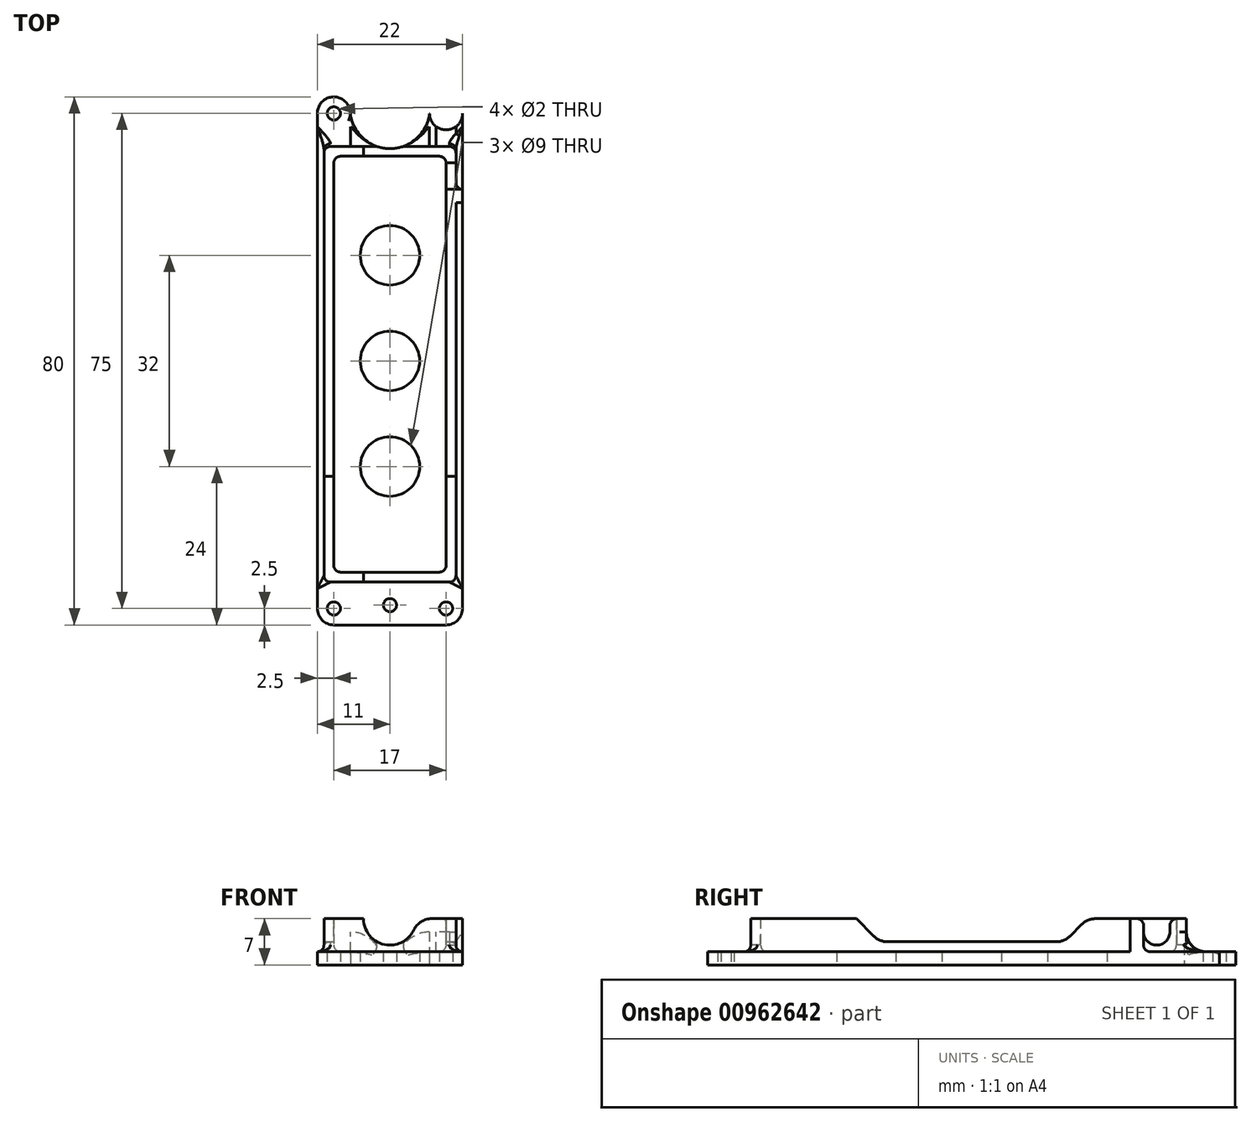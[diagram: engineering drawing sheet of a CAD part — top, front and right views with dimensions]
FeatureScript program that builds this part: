
annotation { "Feature Type Name" : "Feature", "Feature Type Description" : "" }
export const myFeature = defineFeature(function(context is Context, id is Id, definition is map)
    precondition{}
    {
        {
            var Q0;
            Q0=qCreatedBy(makeId("Top.planeOp"),FACE);
            var sketch = newSketch(context, id + "F0", { "sketchPlane" : qUnion([Q0])});
            skPoint(sketch, "E0.middle", {"position": v(0, 0) * mm});
            skPoint(sketch, "E1", {"position": v(-8, 8) * mm});
            skPoint(sketch, "E2", {"position": v(8, 8) * mm});
            skPoint(sketch, "E3", {"position": v(8, -8) * mm});
            skPoint(sketch, "E4", {"position": v(-8, -8) * mm});
            skLineSegment(sketch, "E5", {"start": v(0, -40) * mm, "end": v(8.5, -40) * mm});
            skLineSegment(sketch, "E6", {"start": v(11, -37.5) * mm, "end": v(11, -25.31) * mm});
            skLineSegment(sketch, "E7", {"start": v(-11, 37.5) * mm, "end": v(-11, 25.31) * mm});
            skLineSegment(sketch, "E8", {"start": v(-8.5, -40) * mm, "end": v(0, -40) * mm});
            skLineSegment(sketch, "E9.trimOffspring", {"start": v(11, 25.31) * mm, "end": v(11, 37.5) * mm});
            skLineSegment(sketch, "E10.trimOffspring", {"start": v(-11, -25.31) * mm, "end": v(-11, -37.5) * mm});
            skArc(sketch, "E11.filletArc", {"start": v(-8.5, 40) * mm, "mid": v(-10.27, 39.27) * mm, "end": v(-11, 37.5) * mm});
            skPoint(sketch, "E12.visualSharp", {"position": v(11, 40) * mm});
            skArc(sketch, "E12.filletArc", {"start": v(11, 37.5) * mm, "mid": v(10.27, 39.27) * mm, "end": v(8.5, 40) * mm});
            skArc(sketch, "E13.filletArc", {"start": v(-11, -37.5) * mm, "mid": v(-10.27, -39.27) * mm, "end": v(-8.5, -40) * mm});
            skPoint(sketch, "E14.visualSharp", {"position": v(11, -40) * mm});
            skArc(sketch, "E14.filletArc", {"start": v(8.5, -40) * mm, "mid": v(10.27, -39.27) * mm, "end": v(11, -37.5) * mm});
            skCircle(sketch, "E15", {"center": v(-8.5, 37.5) * mm, "radius": 2.5 * mm});
            skCircle(sketch, "E16", {"center": v(8.5, 37.5) * mm, "radius": 2.5 * mm});
            skCircle(sketch, "E17", {"center": v(-8.5, -37.5) * mm, "radius": 2.5 * mm});
            skCircle(sketch, "E18", {"center": v(8.5, -37.5) * mm, "radius": 2.5 * mm});
            skPoint(sketch, "E19", {"position": v(0, 16) * mm});
            skPoint(sketch, "E20.MirrorP", {"position": v(0, -16) * mm});
            skLineSegment(sketch, "E21", {"start": v(-11, 25.31) * mm, "end": v(-11, -25.31) * mm});
            skLineSegment(sketch, "E22", {"start": v(11, 25.31) * mm, "end": v(11, -25.31) * mm});
            skArc(sketch, "E23", {"start": v(-6, 37.43) * mm, "mid": v(0, 32.15) * mm, "end": v(6, 37.43) * mm});
            skPoint(sketch, "E23.centerSnap0", {"position": v(0, 40) * mm});
            skPoint(sketch, "E24", {"position": v(0, -37) * mm});
            skPoint(sketch, "E25", {"position": v(0, -32) * mm});
            skPoint(sketch, "E26", {"position": v(0, 31) * mm});
            skLineSegment(sketch, "E27", {"start": v(8.5, -32) * mm, "end": v(8.5, 31) * mm});
            skLineSegment(sketch, "E28", {"start": v(0, -32) * mm, "end": v(-8.5, -32) * mm});
            skLineSegment(sketch, "E29", {"start": v(-8.5, -32) * mm, "end": v(-8.5, 31) * mm});
            skLineSegment(sketch, "E30", {"start": v(-8.5, 31) * mm, "end": v(8.5, 31) * mm});
            skLineSegment(sketch, "E31", {"start": v(0, -32) * mm, "end": v(8.5, -32) * mm});
            skLineSegment(sketch, "E32", {"start": v(0, -33.5) * mm, "end": v(10, -33.5) * mm});
            skLineSegment(sketch, "E33", {"start": v(10, -33.5) * mm, "end": v(10, 32.5) * mm});
            skLineSegment(sketch, "E34", {"start": v(10, 32.5) * mm, "end": v(2.03, 32.5) * mm});
            skLineSegment(sketch, "E35.MirrorCS", {"start": v(-10, 32.5) * mm, "end": v(-2.03, 32.5) * mm});
            skLineSegment(sketch, "E36.MirrorCS", {"start": v(-10, -33.5) * mm, "end": v(-10, 32.5) * mm});
            skLineSegment(sketch, "E37.MirrorCS", {"start": v(0, -33.5) * mm, "end": v(-10, -33.5) * mm});
            skPoint(sketch, "E38.orphan", {"position": v(0, 32.5) * mm});
            skSolve(sketch);
        }
        {
            var Q0;
            {var subQ0=sQuery(id+"F0.wireOp",EDGE,"E15");var subQ1=makeQuery(id+"F0.imprint","INTERSECT",VERTEX,{"derivedFrom":[sQuery(id+"F0.wireOp",EDGE,"E7"),subQ0]});Q0=makeQuery(id+"F0.imprint","IMPRINT",FACE,{"disambiguationData":[TD([[makeQuery(id+"F0.imprint","IMPRINT",EDGE,{"disambiguationData":[TD([[subQ1,-1.0]])],"derivedFrom":subQ0}),1.0]])]});}
            var Q1;
            {var subQ3=sQuery(id+"F0.wireOp",EDGE,"E23");Q1=makeQuery(id+"F0.imprint","IMPRINT",FACE,{"disambiguationData":[TD([[makeQuery(id+"F0.imprint","IMPRINT",EDGE,{"derivedFrom":subQ3}),-1.0]])]});}
            var Q2;
            {var subQ0=sQuery(id+"F0.wireOp",EDGE,"E16");var subQ1=makeQuery(id+"F0.imprint","INTERSECT",VERTEX,{"derivedFrom":[sQuery(id+"F0.wireOp",EDGE,"E9.trimOffspring"),subQ0]});Q2=makeQuery(id+"F0.imprint","IMPRINT",FACE,{"disambiguationData":[TD([[makeQuery(id+"F0.imprint","IMPRINT",EDGE,{"disambiguationData":[TD([[subQ1,-1.0]])],"derivedFrom":subQ0}),1.0]])]});}
            var Q3;
            {var subQ3=sQuery(id+"F0.wireOp",EDGE,"E21");Q3=makeQuery(id+"F0.imprint","IMPRINT",FACE,{"disambiguationData":[TD([[makeQuery(id+"F0.imprint","IMPRINT",EDGE,{"derivedFrom":subQ3}),1.0]])]});}
            var Q4;
            Q4=makeQuery(id+"F0.imprint","IMPRINT",FACE,{"disambiguationData":[TD([[makeQuery(id+"F0.imprint","IMPRINT",EDGE,{"derivedFrom":sQuery(id+"F0.wireOp",EDGE,"bMtfzaGi-QSrd-IoLL-XQbp-31UsCRVkDCwl")}),1.0]])]});
            var Q5;
            {var subQ9=sQuery(id+"F0.wireOp",EDGE,"E5");Q5=makeQuery(id+"F0.imprint","IMPRINT",FACE,{"disambiguationData":[TD([[makeQuery(id+"F0.imprint","IMPRINT",EDGE,{"derivedFrom":subQ9}),1.0]])]});}
            var Q6;
            {var subQ0=sQuery(id+"F0.wireOp",EDGE,"E17");var subQ1=makeQuery(id+"F0.imprint","INTERSECT",VERTEX,{"derivedFrom":[sQuery(id+"F0.wireOp",EDGE,"E8"),subQ0]});Q6=makeQuery(id+"F0.imprint","IMPRINT",FACE,{"disambiguationData":[TD([[makeQuery(id+"F0.imprint","IMPRINT",EDGE,{"disambiguationData":[TD([[subQ1,1.0]])],"derivedFrom":subQ0}),1.0]])]});}
            var Q7;
            {var subQ0=sQuery(id+"F0.wireOp",EDGE,"E18");var subQ1=makeQuery(id+"F0.imprint","INTERSECT",VERTEX,{"derivedFrom":[sQuery(id+"F0.wireOp",EDGE,"E5"),subQ0]});Q7=makeQuery(id+"F0.imprint","IMPRINT",FACE,{"disambiguationData":[TD([[makeQuery(id+"F0.imprint","IMPRINT",EDGE,{"disambiguationData":[TD([[subQ1,1.0]])],"derivedFrom":subQ0}),1.0]])]});}
            var Q8;
            Q8=makeQuery(id+"F0.imprint","IMPRINT",FACE,{"disambiguationData":[TD([[makeQuery(id+"F0.imprint","IMPRINT",EDGE,{"derivedFrom":sQuery(id+"F0.wireOp",EDGE,"E27")}),-1.0]])]});
            var Q9;
            Q9=makeQuery(id+"F0.imprint","IMPRINT",FACE,{"disambiguationData":[TD([[makeQuery(id+"F0.imprint","IMPRINT",EDGE,{"derivedFrom":sQuery(id+"F0.wireOp",EDGE,"E27")}),1.0]])]});
            extrude(context, id + "F1", {"entities" : qUnion([Q0, Q1, Q2, Q3, Q4, Q5, Q6, Q7, Q8, Q9]), "depth" : 2 * mm, "offsetDistance" : 25 * mm});
        }
        {
            var Q0;
            Q0=makeQuery(id+"F0.imprint","IMPRINT",FACE,{"disambiguationData":[TD([[makeQuery(id+"F0.imprint","IMPRINT",EDGE,{"derivedFrom":sQuery(id+"F0.wireOp",EDGE,"E27")}),-1.0]])]});
            extrude(context, id + "F2", {"entities" : qUnion([Q0]), "operationType" : NewBodyOperationType.ADD, "depth" : 7 * mm, "offsetDistance" : 25 * mm});
        }
        {
            var Q0;
            Q0=makeQuery(id+"F1.opExtrude","CAP_EDGE",EDGE,{"disambiguationData":[OSD([sQuery(id+"F0.wireOp",EDGE,"E23")])],"isStart":false});
            fillet(context, id + "F3", {"entities" : qUnion([Q0]), "radius" : 0.5 * mm, "tangentPropagation" : true, "allowEdgeOverflow" : false});
        }
        {
            var Q0;
            Q0=makeQuery(id+"F2.opExtrude","SWEPT_EDGE",EDGE,{"disambiguationData":[OSD([sQuery(id+"F0.wireOp",EDGE,"tbeNza1r-utGL-zFzt-WYe0-U05ca4cfrUVO"),sQuery(id+"F0.wireOp",EDGE,"CjghIOQ9-IqcJ-TMon-Jhqv-waYeZpEdJ196")])]});
            var Q1;
            Q1=makeQuery(id+"F2.opExtrude","SWEPT_EDGE",EDGE,{"disambiguationData":[OSD([sQuery(id+"F0.wireOp",EDGE,"bMtfzaGi-QSrd-IoLL-XQbp-31UsCRVkDCwl"),sQuery(id+"F0.wireOp",EDGE,"sX6MG20U-e8zL-cwBF-vJcw-WzJNnX85c195")])]});
            var Q2;
            Q2=makeQuery(id+"F2.opExtrude","SWEPT_EDGE",EDGE,{"disambiguationData":[OSD([sQuery(id+"F0.wireOp",EDGE,"sX6MG20U-e8zL-cwBF-vJcw-WzJNnX85c195"),sQuery(id+"F0.wireOp",EDGE,"Iet94KMb-kpEY-E7AR-qc5a-OqAxkwTAn5af")])]});
            var Q3;
            Q3=makeQuery(id+"F2.opExtrude","SWEPT_EDGE",EDGE,{"disambiguationData":[OSD([sQuery(id+"F0.wireOp",EDGE,"Iet94KMb-kpEY-E7AR-qc5a-OqAxkwTAn5af"),sQuery(id+"F0.wireOp",EDGE,"tbeNza1r-utGL-zFzt-WYe0-U05ca4cfrUVO")])]});
            var Q4;
            Q4=makeQuery(id+"F2.boolean.opBoolean","INTERSECT",EDGE,{"derivedFrom":[makeQuery(id+"F1.opExtrude","CAP_FACE",FACE,{"disambiguationData":[OSD([sQuery(id+"F0.wireOp",EDGE,"E5"),sQuery(id+"F0.wireOp",EDGE,"E6"),sQuery(id+"F0.wireOp",EDGE,"E7"),sQuery(id+"F0.wireOp",EDGE,"E8"),sQuery(id+"F0.wireOp",EDGE,"E9.trimOffspring"),sQuery(id+"F0.wireOp",EDGE,"E10.trimOffspring"),sQuery(id+"F0.wireOp",EDGE,"E15"),sQuery(id+"F0.wireOp",EDGE,"E16"),sQuery(id+"F0.wireOp",EDGE,"E17"),sQuery(id+"F0.wireOp",EDGE,"E18"),sQuery(id+"F0.wireOp",EDGE,"E21"),sQuery(id+"F0.wireOp",EDGE,"E22"),sQuery(id+"F0.wireOp",EDGE,"E23")])],"isStart":false}),makeQuery(id+"F2.opExtrude","SWEPT_FACE",FACE,{"disambiguationData":[OSD([sQuery(id+"F0.wireOp",EDGE,"E27")])]})]});
            var Q5;
            Q5=makeQuery(id+"F2.boolean.opBoolean","INTERSECT",EDGE,{"derivedFrom":[makeQuery(id+"F1.opExtrude","CAP_FACE",FACE,{"disambiguationData":[OSD([sQuery(id+"F0.wireOp",EDGE,"E5"),sQuery(id+"F0.wireOp",EDGE,"E6"),sQuery(id+"F0.wireOp",EDGE,"E7"),sQuery(id+"F0.wireOp",EDGE,"E8"),sQuery(id+"F0.wireOp",EDGE,"E9.trimOffspring"),sQuery(id+"F0.wireOp",EDGE,"E10.trimOffspring"),sQuery(id+"F0.wireOp",EDGE,"E15"),sQuery(id+"F0.wireOp",EDGE,"E16"),sQuery(id+"F0.wireOp",EDGE,"E17"),sQuery(id+"F0.wireOp",EDGE,"E18"),sQuery(id+"F0.wireOp",EDGE,"E21"),sQuery(id+"F0.wireOp",EDGE,"E22"),sQuery(id+"F0.wireOp",EDGE,"E23")])],"isStart":false}),makeQuery(id+"F2.opExtrude","SWEPT_FACE",FACE,{"disambiguationData":[OSD([sQuery(id+"F0.wireOp",EDGE,"E28"),sQuery(id+"F0.wireOp",EDGE,"E31")])]})]});
            var Q6;
            Q6=makeQuery(id+"F2.boolean.opBoolean","INTERSECT",EDGE,{"derivedFrom":[makeQuery(id+"F1.opExtrude","CAP_FACE",FACE,{"disambiguationData":[OSD([sQuery(id+"F0.wireOp",EDGE,"E5"),sQuery(id+"F0.wireOp",EDGE,"E6"),sQuery(id+"F0.wireOp",EDGE,"E7"),sQuery(id+"F0.wireOp",EDGE,"E8"),sQuery(id+"F0.wireOp",EDGE,"E9.trimOffspring"),sQuery(id+"F0.wireOp",EDGE,"E10.trimOffspring"),sQuery(id+"F0.wireOp",EDGE,"E15"),sQuery(id+"F0.wireOp",EDGE,"E16"),sQuery(id+"F0.wireOp",EDGE,"E17"),sQuery(id+"F0.wireOp",EDGE,"E18"),sQuery(id+"F0.wireOp",EDGE,"E21"),sQuery(id+"F0.wireOp",EDGE,"E22"),sQuery(id+"F0.wireOp",EDGE,"E23")])],"isStart":false}),makeQuery(id+"F2.opExtrude","SWEPT_FACE",FACE,{"disambiguationData":[OSD([sQuery(id+"F0.wireOp",EDGE,"E29")])]})]});
            var Q7;
            Q7=makeQuery(id+"F2.boolean.opBoolean","INTERSECT",EDGE,{"derivedFrom":[makeQuery(id+"F1.opExtrude","CAP_FACE",FACE,{"disambiguationData":[OSD([sQuery(id+"F0.wireOp",EDGE,"E5"),sQuery(id+"F0.wireOp",EDGE,"E6"),sQuery(id+"F0.wireOp",EDGE,"E7"),sQuery(id+"F0.wireOp",EDGE,"E8"),sQuery(id+"F0.wireOp",EDGE,"E9.trimOffspring"),sQuery(id+"F0.wireOp",EDGE,"E10.trimOffspring"),sQuery(id+"F0.wireOp",EDGE,"E15"),sQuery(id+"F0.wireOp",EDGE,"E16"),sQuery(id+"F0.wireOp",EDGE,"E17"),sQuery(id+"F0.wireOp",EDGE,"E18"),sQuery(id+"F0.wireOp",EDGE,"E21"),sQuery(id+"F0.wireOp",EDGE,"E22"),sQuery(id+"F0.wireOp",EDGE,"E23")])],"isStart":false}),makeQuery(id+"F2.opExtrude","SWEPT_FACE",FACE,{"disambiguationData":[OSD([sQuery(id+"F0.wireOp",EDGE,"E30")])]})]});
            var Q8;
            Q8=makeQuery(id+"F2.boolean.opBoolean","INTERSECT",EDGE,{"derivedFrom":[makeQuery(id+"F1.opExtrude","CAP_FACE",FACE,{"disambiguationData":[OSD([sQuery(id+"F0.wireOp",EDGE,"E5"),sQuery(id+"F0.wireOp",EDGE,"E6"),sQuery(id+"F0.wireOp",EDGE,"E7"),sQuery(id+"F0.wireOp",EDGE,"E8"),sQuery(id+"F0.wireOp",EDGE,"E9.trimOffspring"),sQuery(id+"F0.wireOp",EDGE,"E10.trimOffspring"),sQuery(id+"F0.wireOp",EDGE,"E15"),sQuery(id+"F0.wireOp",EDGE,"E16"),sQuery(id+"F0.wireOp",EDGE,"E17"),sQuery(id+"F0.wireOp",EDGE,"E18"),sQuery(id+"F0.wireOp",EDGE,"E21"),sQuery(id+"F0.wireOp",EDGE,"E22"),sQuery(id+"F0.wireOp",EDGE,"E23")])],"isStart":false}),makeQuery(id+"F2.opExtrude","SWEPT_FACE",FACE,{"disambiguationData":[OSD([sQuery(id+"F0.wireOp",EDGE,"E32"),sQuery(id+"F0.wireOp",EDGE,"E37.MirrorCS")])]})]});
            var Q9;
            Q9=makeQuery(id+"F2.boolean.opBoolean","INTERSECT",EDGE,{"derivedFrom":[makeQuery(id+"F1.opExtrude","CAP_FACE",FACE,{"disambiguationData":[OSD([sQuery(id+"F0.wireOp",EDGE,"E5"),sQuery(id+"F0.wireOp",EDGE,"E6"),sQuery(id+"F0.wireOp",EDGE,"E7"),sQuery(id+"F0.wireOp",EDGE,"E8"),sQuery(id+"F0.wireOp",EDGE,"E9.trimOffspring"),sQuery(id+"F0.wireOp",EDGE,"E10.trimOffspring"),sQuery(id+"F0.wireOp",EDGE,"E15"),sQuery(id+"F0.wireOp",EDGE,"E16"),sQuery(id+"F0.wireOp",EDGE,"E17"),sQuery(id+"F0.wireOp",EDGE,"E18"),sQuery(id+"F0.wireOp",EDGE,"E21"),sQuery(id+"F0.wireOp",EDGE,"E22"),sQuery(id+"F0.wireOp",EDGE,"E23")])],"isStart":false}),makeQuery(id+"F2.opExtrude","SWEPT_FACE",FACE,{"disambiguationData":[OSD([sQuery(id+"F0.wireOp",EDGE,"E33")])]})]});
            var Q10;
            Q10=makeQuery(id+"F2.boolean.opBoolean","INTERSECT",EDGE,{"derivedFrom":[makeQuery(id+"F1.opExtrude","CAP_FACE",FACE,{"disambiguationData":[OSD([sQuery(id+"F0.wireOp",EDGE,"E5"),sQuery(id+"F0.wireOp",EDGE,"E6"),sQuery(id+"F0.wireOp",EDGE,"E7"),sQuery(id+"F0.wireOp",EDGE,"E8"),sQuery(id+"F0.wireOp",EDGE,"E9.trimOffspring"),sQuery(id+"F0.wireOp",EDGE,"E10.trimOffspring"),sQuery(id+"F0.wireOp",EDGE,"E15"),sQuery(id+"F0.wireOp",EDGE,"E16"),sQuery(id+"F0.wireOp",EDGE,"E17"),sQuery(id+"F0.wireOp",EDGE,"E18"),sQuery(id+"F0.wireOp",EDGE,"E21"),sQuery(id+"F0.wireOp",EDGE,"E22"),sQuery(id+"F0.wireOp",EDGE,"E23")])],"isStart":false}),makeQuery(id+"F2.opExtrude","SWEPT_FACE",FACE,{"disambiguationData":[OSD([sQuery(id+"F0.wireOp",EDGE,"E36.MirrorCS")])]})]});
            fillet(context, id + "F4", {"entities" : qUnion([Q0, Q1, Q2, Q3, Q4, Q5, Q6, Q7, Q8, Q9, Q10]), "radius" : 1 * mm, "tangentPropagation" : true, "allowEdgeOverflow" : false});
        }
        {
            var Q0;
            Q0=makeQuery(id+"F2.opExtrude","SWEPT_FACE",FACE,{"disambiguationData":[OSD([sQuery(id+"F0.wireOp",EDGE,"E36.MirrorCS")])]});
            var sketch = newSketch(context, id + "F5", { "sketchPlane" : qUnion([Q0])});
            skLineSegment(sketch, "E39", {"start": v(0, 0) * mm, "end": v(0, 3.5) * mm});
            skLineSegment(sketch, "E40", {"start": v(0, 3.5) * mm, "end": v(14, 3.5) * mm});
            skLineSegment(sketch, "E41", {"start": v(17.5, 7) * mm, "end": v(14, 3.5) * mm});
            skLineSegment(sketch, "E42.MirrorCS", {"start": v(0, 3.5) * mm, "end": v(-14, 3.5) * mm});
            skLineSegment(sketch, "E43.MirrorCS", {"start": v(-17.5, 7) * mm, "end": v(-14, 3.5) * mm});
            skSolve(sketch);
        }
        {
            var Q0;
            Q0=makeQuery(id+"F5.imprint","IMPRINT",FACE,{"disambiguationData":[TD([[makeQuery(id+"F5.imprint","IMPRINT",EDGE,{"derivedFrom":sQuery(id+"F5.wireOp",EDGE,"E40")}),1.0]])]});
            extrude(context, id + "F6", {"entities" : qUnion([Q0]), "operationType" : NewBodyOperationType.REMOVE, "depth" : 25 * mm, "offsetDistance" : 25 * mm, "hasSecondDirection" : true, "secondDirectionOppositeDirection" : true, "secondDirectionDepth" : 25 * mm});
        }
        {
            var Q0;
            Q0=sQuery(id+"F0.wireOp",VERTEX,"E12.filletArc.center");
            var Q1;
            Q1=sQuery(id+"F0.wireOp",VERTEX,"E11.filletArc.center");
            var Q2;
            Q2=sQuery(id+"F0.wireOp",VERTEX,"E14.filletArc.center");
            var Q3;
            Q3=sQuery(id+"F0.wireOp",VERTEX,"E13.filletArc.center");
            var Q4;
            Q4=sQuery(id+"F0.wireOp",VERTEX,"E24");
            var Q5;
            Q5=makeQuery(id+"F1.opExtrude","SWEPT_BODY",BODY,{"disambiguationData":[OSD([sQuery(id+"F0.wireOp",EDGE,"E5"),sQuery(id+"F0.wireOp",EDGE,"E6"),sQuery(id+"F0.wireOp",EDGE,"E7"),sQuery(id+"F0.wireOp",EDGE,"E8"),sQuery(id+"F0.wireOp",EDGE,"E9.trimOffspring"),sQuery(id+"F0.wireOp",EDGE,"E10.trimOffspring"),sQuery(id+"F0.wireOp",EDGE,"E15"),sQuery(id+"F0.wireOp",EDGE,"E16"),sQuery(id+"F0.wireOp",EDGE,"E17"),sQuery(id+"F0.wireOp",EDGE,"E18"),sQuery(id+"F0.wireOp",EDGE,"E21"),sQuery(id+"F0.wireOp",EDGE,"E22"),sQuery(id+"F0.wireOp",EDGE,"E23")])]});
            hole(context, id + "F7", {"style" : HoleStyle.SIMPLE, "endStyle" : HoleEndStyle.BLIND, "oppositeDirection" : true, "holeDiameter" : 2 * mm, "majorDiameter" : 5 * mm, "holeDepth" : 7 * mm, "isTappedThrough" : true, "tappedDepth" : 12 * mm, "tapClearance" : 3, "startFromSketch" : true, "locations" : qUnion([Q0, Q1, Q2, Q3, Q4]), "scope" : qUnion([Q5])});
        }
        {
            var Q0;
            Q0=sQuery(id+"F0.wireOp",VERTEX,"E19");
            var Q1;
            Q1=sQuery(id+"F0.wireOp",VERTEX,"E20.MirrorP");
            var Q2;
            Q2=sQuery(id+"F0.wireOp",VERTEX,"E0.middle");
            var Q3;
            Q3=makeQuery(id+"F1.opExtrude","SWEPT_BODY",BODY,{"disambiguationData":[OSD([sQuery(id+"F0.wireOp",EDGE,"E5"),sQuery(id+"F0.wireOp",EDGE,"E6"),sQuery(id+"F0.wireOp",EDGE,"E7"),sQuery(id+"F0.wireOp",EDGE,"E8"),sQuery(id+"F0.wireOp",EDGE,"E9.trimOffspring"),sQuery(id+"F0.wireOp",EDGE,"E10.trimOffspring"),sQuery(id+"F0.wireOp",EDGE,"E15"),sQuery(id+"F0.wireOp",EDGE,"E16"),sQuery(id+"F0.wireOp",EDGE,"E17"),sQuery(id+"F0.wireOp",EDGE,"E18"),sQuery(id+"F0.wireOp",EDGE,"E21"),sQuery(id+"F0.wireOp",EDGE,"E22"),sQuery(id+"F0.wireOp",EDGE,"E23")])]});
            hole(context, id + "F8", {"style" : HoleStyle.SIMPLE, "endStyle" : HoleEndStyle.BLIND, "oppositeDirection" : true, "holeDiameter" : 9 * mm, "majorDiameter" : 5 * mm, "holeDepth" : 7 * mm, "isTappedThrough" : true, "tappedDepth" : 12 * mm, "tapClearance" : 3, "startFromSketch" : true, "locations" : qUnion([Q0, Q1, Q2]), "scope" : qUnion([Q3])});
        }
        {
            var Q0;
            Q0=makeQuery(id+"F2.boolean.opBoolean","INTERSECT",EDGE,{"derivedFrom":[makeQuery(id+"F1.opExtrude","CAP_FACE",FACE,{"disambiguationData":[OSD([sQuery(id+"F0.wireOp",EDGE,"E5"),sQuery(id+"F0.wireOp",EDGE,"E6"),sQuery(id+"F0.wireOp",EDGE,"E7"),sQuery(id+"F0.wireOp",EDGE,"E8"),sQuery(id+"F0.wireOp",EDGE,"E9.trimOffspring"),sQuery(id+"F0.wireOp",EDGE,"E10.trimOffspring"),sQuery(id+"F0.wireOp",EDGE,"E15"),sQuery(id+"F0.wireOp",EDGE,"E16"),sQuery(id+"F0.wireOp",EDGE,"E17"),sQuery(id+"F0.wireOp",EDGE,"E18"),sQuery(id+"F0.wireOp",EDGE,"E21"),sQuery(id+"F0.wireOp",EDGE,"E22"),sQuery(id+"F0.wireOp",EDGE,"E23")])],"isStart":false}),makeQuery(id+"F2.opExtrude","SWEPT_FACE",FACE,{"disambiguationData":[OSD([sQuery(id+"F0.wireOp",EDGE,"E35.MirrorCS")])]})]});
            var Q1;
            Q1=makeQuery(id+"F2.boolean.opBoolean","INTERSECT",EDGE,{"derivedFrom":[makeQuery(id+"F1.opExtrude","CAP_FACE",FACE,{"disambiguationData":[OSD([sQuery(id+"F0.wireOp",EDGE,"E5"),sQuery(id+"F0.wireOp",EDGE,"E6"),sQuery(id+"F0.wireOp",EDGE,"E7"),sQuery(id+"F0.wireOp",EDGE,"E8"),sQuery(id+"F0.wireOp",EDGE,"E9.trimOffspring"),sQuery(id+"F0.wireOp",EDGE,"E10.trimOffspring"),sQuery(id+"F0.wireOp",EDGE,"E15"),sQuery(id+"F0.wireOp",EDGE,"E16"),sQuery(id+"F0.wireOp",EDGE,"E17"),sQuery(id+"F0.wireOp",EDGE,"E18"),sQuery(id+"F0.wireOp",EDGE,"E21"),sQuery(id+"F0.wireOp",EDGE,"E22"),sQuery(id+"F0.wireOp",EDGE,"E23")])],"isStart":false}),makeQuery(id+"F2.opExtrude","SWEPT_FACE",FACE,{"disambiguationData":[OSD([sQuery(id+"F0.wireOp",EDGE,"E34")])]})]});
            fillet(context, id + "F9", {"entities" : qUnion([Q0, Q1]), "radius" : 3 * mm, "tangentPropagation" : true, "allowEdgeOverflow" : false});
        }
        {
            var Q0;
            Q0=makeQuery(id+"F2.opExtrude","SWEPT_FACE",FACE,{"disambiguationData":[OSD([sQuery(id+"F0.wireOp",EDGE,"E32"),sQuery(id+"F0.wireOp",EDGE,"E37.MirrorCS")])]});
            var sketch = newSketch(context, id + "F10", { "sketchPlane" : qUnion([Q0])});
            skLineSegment(sketch, "E44", {"start": v(0, 0) * mm, "end": v(0, 7) * mm});
            skCircle(sketch, "E45", {"center": v(0, 7) * mm, "radius": 4 * mm});
            skSolve(sketch);
        }
        {
            var Q0;
            {var subQ0=sQuery(id+"F10.wireOp",EDGE,"E44");var subQ1=sQuery(id+"F0.wireOp",EDGE,"E37.MirrorCS");var subQ2=sQuery(id+"F0.wireOp",EDGE,"E32");var subQ3=makeQuery(id+"F2.opExtrude","CAP_EDGE",EDGE,{"disambiguationData":[OSD([subQ2,subQ1])],"isStart":false});var subQ4=makeQuery(id+"F10.imprint","INTERSECT",VERTEX,{"derivedFrom":[subQ3,subQ0]});Q0=makeQuery(id+"F10.imprint","IMPRINT",FACE,{"disambiguationData":[TD([[makeQuery(id+"F10.imprint","IMPRINT",EDGE,{"disambiguationData":[TD([[subQ4,-1.0]])],"derivedFrom":subQ3}),1.0]])]});}
            var Q1;
            {var subQ0=sQuery(id+"F10.wireOp",EDGE,"E44");var subQ1=sQuery(id+"F0.wireOp",EDGE,"E37.MirrorCS");var subQ2=sQuery(id+"F0.wireOp",EDGE,"E32");var subQ3=makeQuery(id+"F2.opExtrude","CAP_EDGE",EDGE,{"disambiguationData":[OSD([subQ2,subQ1])],"isStart":false});var subQ4=makeQuery(id+"F10.imprint","INTERSECT",VERTEX,{"derivedFrom":[subQ3,subQ0]});Q1=makeQuery(id+"F10.imprint","IMPRINT",FACE,{"disambiguationData":[TD([[makeQuery(id+"F10.imprint","IMPRINT",EDGE,{"disambiguationData":[TD([[subQ4,1.0]])],"derivedFrom":subQ3}),1.0]])]});}
            extrude(context, id + "F11", {"entities" : qUnion([Q0, Q1]), "operationType" : NewBodyOperationType.REMOVE, "oppositeDirection" : true, "depth" : 80 * mm, "offsetDistance" : 25 * mm});
        }
        {
            var Q0;
            {var subQ0=sQuery(id+"F0.wireOp",EDGE,"E37.MirrorCS");var subQ1=sQuery(id+"F0.wireOp",EDGE,"E32");var subQ2=sQuery(id+"F0.wireOp",EDGE,"E31");var subQ3=sQuery(id+"F0.wireOp",EDGE,"E28");var subQ4=sQuery(id+"F10.wireOp",EDGE,"E45");Q0=makeQuery(id+"F11.boolean.opBoolean","COPY",EDGE,{"disambiguationData":[TD([makeQuery(id+"F2.opExtrude","SWEPT_FACE",FACE,{"disambiguationData":[OSD([subQ3,subQ2])]})])],"derivedFrom":makeQuery(id+"F11.opExtrude","SWEPT_EDGE",EDGE,{"disambiguationData":[OSD([subQ1,subQ0,subQ4]),TDD([makeQuery(id+"F10.imprint","INTERSECT",VERTEX,{"disambiguationData":[OD(1.0)],"derivedFrom":[makeQuery(id+"F2.opExtrude","CAP_EDGE",EDGE,{"disambiguationData":[OSD([subQ1,subQ0])],"isStart":false}),subQ4]})])]})});}
            var Q1;
            {var subQ0=sQuery(id+"F0.wireOp",EDGE,"E37.MirrorCS");var subQ1=sQuery(id+"F0.wireOp",EDGE,"E32");var subQ2=sQuery(id+"F0.wireOp",EDGE,"E31");var subQ3=sQuery(id+"F0.wireOp",EDGE,"E28");var subQ4=sQuery(id+"F10.wireOp",EDGE,"E45");Q1=makeQuery(id+"F11.boolean.opBoolean","COPY",EDGE,{"disambiguationData":[TD([makeQuery(id+"F2.opExtrude","SWEPT_FACE",FACE,{"disambiguationData":[OSD([subQ3,subQ2])]})])],"derivedFrom":makeQuery(id+"F11.opExtrude","SWEPT_EDGE",EDGE,{"disambiguationData":[OSD([subQ1,subQ0,subQ4]),TDD([makeQuery(id+"F10.imprint","INTERSECT",VERTEX,{"disambiguationData":[OD(0.0)],"derivedFrom":[makeQuery(id+"F2.opExtrude","CAP_EDGE",EDGE,{"disambiguationData":[OSD([subQ1,subQ0])],"isStart":false}),subQ4]})])]})});}
            var Q2;
            {var subQ0=sQuery(id+"F0.wireOp",EDGE,"E36.MirrorCS");var subQ2=sQuery(id+"F0.wireOp",EDGE,"E27");var subQ3=sQuery(id+"F5.wireOp",EDGE,"E41");Q2=makeQuery(id+"F6.boolean.opBoolean","COPY",EDGE,{"disambiguationData":[TD([makeQuery(id+"F2.opExtrude","SWEPT_FACE",FACE,{"disambiguationData":[OSD([subQ2])]})])],"derivedFrom":makeQuery(id+"F6.opExtrude","SWEPT_EDGE",EDGE,{"disambiguationData":[OSD([subQ0,subQ3])]})});}
            var Q3;
            {var subQ0=sQuery(id+"F5.wireOp",EDGE,"E40");var subQ1=sQuery(id+"F5.wireOp",EDGE,"E41");Q3=makeQuery(id+"F6.boolean.opBoolean","COPY",EDGE,{"disambiguationData":[TD([makeQuery(id+"F2.opExtrude","SWEPT_FACE",FACE,{"disambiguationData":[OSD([sQuery(id+"F0.wireOp",EDGE,"E27")])]})])],"derivedFrom":makeQuery(id+"F6.opExtrude","SWEPT_EDGE",EDGE,{"disambiguationData":[OSD([subQ0,subQ1])]})});}
            var Q4;
            {var subQ0=sQuery(id+"F5.wireOp",EDGE,"E42.MirrorCS");var subQ1=sQuery(id+"F5.wireOp",EDGE,"E43.MirrorCS");Q4=makeQuery(id+"F6.boolean.opBoolean","COPY",EDGE,{"disambiguationData":[TD([makeQuery(id+"F2.opExtrude","SWEPT_FACE",FACE,{"disambiguationData":[OSD([sQuery(id+"F0.wireOp",EDGE,"E27")])]})])],"derivedFrom":makeQuery(id+"F6.opExtrude","SWEPT_EDGE",EDGE,{"disambiguationData":[OSD([subQ0,subQ1])]})});}
            var Q5;
            {var subQ0=sQuery(id+"F0.wireOp",EDGE,"E36.MirrorCS");var subQ2=sQuery(id+"F0.wireOp",EDGE,"E27");var subQ3=sQuery(id+"F5.wireOp",EDGE,"E43.MirrorCS");Q5=makeQuery(id+"F6.boolean.opBoolean","COPY",EDGE,{"disambiguationData":[TD([makeQuery(id+"F2.opExtrude","SWEPT_FACE",FACE,{"disambiguationData":[OSD([subQ2])]})])],"derivedFrom":makeQuery(id+"F6.opExtrude","SWEPT_EDGE",EDGE,{"disambiguationData":[OSD([subQ0,subQ3])]})});}
            var Q6;
            {var subQ0=sQuery(id+"F0.wireOp",EDGE,"E37.MirrorCS");var subQ2=sQuery(id+"F0.wireOp",EDGE,"E32");var subQ3=sQuery(id+"F0.wireOp",EDGE,"E30");var subQ4=sQuery(id+"F10.wireOp",EDGE,"E45");Q6=makeQuery(id+"F11.boolean.opBoolean","COPY",EDGE,{"disambiguationData":[TD([makeQuery(id+"F2.opExtrude","SWEPT_FACE",FACE,{"disambiguationData":[OSD([subQ3])]})])],"derivedFrom":makeQuery(id+"F11.opExtrude","SWEPT_EDGE",EDGE,{"disambiguationData":[OSD([subQ2,subQ0,subQ4]),TDD([makeQuery(id+"F10.imprint","INTERSECT",VERTEX,{"disambiguationData":[OD(1.0)],"derivedFrom":[makeQuery(id+"F2.opExtrude","CAP_EDGE",EDGE,{"disambiguationData":[OSD([subQ2,subQ0])],"isStart":false}),subQ4]})])]})});}
            var Q7;
            {var subQ0=sQuery(id+"F0.wireOp",EDGE,"E37.MirrorCS");var subQ2=sQuery(id+"F0.wireOp",EDGE,"E32");var subQ3=sQuery(id+"F0.wireOp",EDGE,"E30");var subQ4=sQuery(id+"F10.wireOp",EDGE,"E45");Q7=makeQuery(id+"F11.boolean.opBoolean","COPY",EDGE,{"disambiguationData":[TD([makeQuery(id+"F2.opExtrude","SWEPT_FACE",FACE,{"disambiguationData":[OSD([subQ3])]})])],"derivedFrom":makeQuery(id+"F11.opExtrude","SWEPT_EDGE",EDGE,{"disambiguationData":[OSD([subQ2,subQ0,subQ4]),TDD([makeQuery(id+"F10.imprint","INTERSECT",VERTEX,{"disambiguationData":[OD(0.0)],"derivedFrom":[makeQuery(id+"F2.opExtrude","CAP_EDGE",EDGE,{"disambiguationData":[OSD([subQ2,subQ0])],"isStart":false}),subQ4]})])]})});}
            var Q8;
            {var subQ0=sQuery(id+"F0.wireOp",EDGE,"E36.MirrorCS");var subQ1=sQuery(id+"F0.wireOp",EDGE,"E29");var subQ2=sQuery(id+"F5.wireOp",EDGE,"E43.MirrorCS");Q8=makeQuery(id+"F6.boolean.opBoolean","COPY",EDGE,{"disambiguationData":[TD([makeQuery(id+"F2.opExtrude","SWEPT_FACE",FACE,{"disambiguationData":[OSD([subQ1])]})])],"derivedFrom":makeQuery(id+"F6.opExtrude","SWEPT_EDGE",EDGE,{"disambiguationData":[OSD([subQ0,subQ2])]})});}
            var Q9;
            {var subQ0=sQuery(id+"F5.wireOp",EDGE,"E43.MirrorCS");var subQ1=sQuery(id+"F5.wireOp",EDGE,"E42.MirrorCS");Q9=makeQuery(id+"F6.boolean.opBoolean","COPY",EDGE,{"disambiguationData":[TD([makeQuery(id+"F2.opExtrude","SWEPT_FACE",FACE,{"disambiguationData":[OSD([sQuery(id+"F0.wireOp",EDGE,"E29")])]})])],"derivedFrom":makeQuery(id+"F6.opExtrude","SWEPT_EDGE",EDGE,{"disambiguationData":[OSD([subQ1,subQ0])]})});}
            var Q10;
            {var subQ0=sQuery(id+"F5.wireOp",EDGE,"E40");var subQ1=sQuery(id+"F5.wireOp",EDGE,"E41");Q10=makeQuery(id+"F6.boolean.opBoolean","COPY",EDGE,{"disambiguationData":[TD([makeQuery(id+"F2.opExtrude","SWEPT_FACE",FACE,{"disambiguationData":[OSD([sQuery(id+"F0.wireOp",EDGE,"E29")])]})])],"derivedFrom":makeQuery(id+"F6.opExtrude","SWEPT_EDGE",EDGE,{"disambiguationData":[OSD([subQ0,subQ1])]})});}
            var Q11;
            {var subQ0=sQuery(id+"F0.wireOp",EDGE,"E36.MirrorCS");var subQ1=sQuery(id+"F0.wireOp",EDGE,"E29");var subQ2=sQuery(id+"F5.wireOp",EDGE,"E41");Q11=makeQuery(id+"F6.boolean.opBoolean","COPY",EDGE,{"disambiguationData":[TD([makeQuery(id+"F2.opExtrude","SWEPT_FACE",FACE,{"disambiguationData":[OSD([subQ1])]})])],"derivedFrom":makeQuery(id+"F6.opExtrude","SWEPT_EDGE",EDGE,{"disambiguationData":[OSD([subQ0,subQ2])]})});}
            fillet(context, id + "F12", {"entities" : qUnion([Q0, Q1, Q2, Q3, Q4, Q5, Q6, Q7, Q8, Q9, Q10, Q11]), "radius" : (3) * mm, "tangentPropagation" : true, "allowEdgeOverflow" : false});
        }
        {
            var Q0;
            Q0=makeQuery(id+"F2.opExtrude","SWEPT_EDGE",EDGE,{"disambiguationData":[OSD([sQuery(id+"F0.wireOp",EDGE,"E35.MirrorCS"),sQuery(id+"F0.wireOp",EDGE,"E36.MirrorCS")])]});
            var Q1;
            Q1=makeQuery(id+"F2.opExtrude","SWEPT_EDGE",EDGE,{"disambiguationData":[OSD([sQuery(id+"F0.wireOp",EDGE,"E33"),sQuery(id+"F0.wireOp",EDGE,"E34")])]});
            var Q2;
            Q2=makeQuery(id+"F2.opExtrude","SWEPT_EDGE",EDGE,{"disambiguationData":[OSD([sQuery(id+"F0.wireOp",EDGE,"E27"),sQuery(id+"F0.wireOp",EDGE,"E30")])]});
            var Q3;
            Q3=makeQuery(id+"F2.opExtrude","SWEPT_EDGE",EDGE,{"disambiguationData":[OSD([sQuery(id+"F0.wireOp",EDGE,"E29"),sQuery(id+"F0.wireOp",EDGE,"E30")])]});
            var Q4;
            Q4=makeQuery(id+"F2.opExtrude","SWEPT_EDGE",EDGE,{"disambiguationData":[OSD([sQuery(id+"F0.wireOp",EDGE,"E32"),sQuery(id+"F0.wireOp",EDGE,"E33")])]});
            var Q5;
            Q5=makeQuery(id+"F2.opExtrude","SWEPT_EDGE",EDGE,{"disambiguationData":[OSD([sQuery(id+"F0.wireOp",EDGE,"E36.MirrorCS"),sQuery(id+"F0.wireOp",EDGE,"E37.MirrorCS")])]});
            var Q6;
            Q6=makeQuery(id+"F2.opExtrude","SWEPT_EDGE",EDGE,{"disambiguationData":[OSD([sQuery(id+"F0.wireOp",EDGE,"E27"),sQuery(id+"F0.wireOp",EDGE,"E31")])]});
            var Q7;
            Q7=makeQuery(id+"F2.opExtrude","SWEPT_EDGE",EDGE,{"disambiguationData":[OSD([sQuery(id+"F0.wireOp",EDGE,"E28"),sQuery(id+"F0.wireOp",EDGE,"E29")])]});
            fillet(context, id + "F13", {"entities" : qUnion([Q0, Q1, Q2, Q3, Q4, Q5, Q6, Q7]), "radius" : 1 * mm, "tangentPropagation" : true, "allowEdgeOverflow" : false});
        }
        {
            var Q0;
            Q0=makeQuery(id+"F2.opExtrude","SWEPT_FACE",FACE,{"disambiguationData":[OSD([sQuery(id+"F0.wireOp",EDGE,"E33")])]});
            var sketch = newSketch(context, id + "F14", { "sketchPlane" : qUnion([Q0])});
            skLineSegment(sketch, "E46", {"start": v(0, 0) * mm, "end": v(28, 0) * mm});
            skLineSegment(sketch, "E47", {"start": v(28, 0) * mm, "end": v(28, 5) * mm});
            skArc(sketch, "E48", {"start": v(26, 5) * mm, "mid": v(28, 3) * mm, "end": v(30, 5) * mm});
            skLineSegment(sketch, "E49", {"start": v(30, 5) * mm, "end": v(30, 7) * mm});
            skLineSegment(sketch, "E50.MirrorCS", {"start": v(26, 5) * mm, "end": v(26, 7) * mm});
            skLineSegment(sketch, "E51", {"start": v(26, 7) * mm, "end": v(30, 7) * mm});
            skLineSegment(sketch, "E52", {"start": v(26, 7) * mm, "end": v(24, 7) * mm});
            skLineSegment(sketch, "E53", {"start": v(24, 7) * mm, "end": v(24, 2) * mm});
            skLineSegment(sketch, "E54", {"start": v(24, 2) * mm, "end": v(26, 2) * mm});
            skLineSegment(sketch, "E55", {"start": v(26, 2) * mm, "end": v(26, 5) * mm});
            skSolve(sketch);
        }
        {
            var Q0;
            {var subQ1=sQuery(id+"F14.wireOp",EDGE,"E49");Q0=makeQuery(id+"F14.imprint","IMPRINT",FACE,{"disambiguationData":[TD([[makeQuery(id+"F14.imprint","IMPRINT",EDGE,{"derivedFrom":subQ1}),1.0]])]});}
            extrude(context, id + "F15", {"entities" : qUnion([Q0]), "operationType" : NewBodyOperationType.REMOVE, "oppositeDirection" : true, "depth" : 5 * mm, "offsetDistance" : 25 * mm});
        }
        {
            var Q0;
            {var subQ9=sQuery(id+"F14.wireOp",EDGE,"E50.MirrorCS");Q0=makeQuery(id+"F14.imprint","IMPRINT",FACE,{"disambiguationData":[TD([[makeQuery(id+"F14.imprint","IMPRINT",EDGE,{"derivedFrom":subQ9}),1.0]])]});}
            var Q1;
            {var subQ0=sQuery(id+"F14.wireOp",EDGE,"E54");Q1=makeQuery(id+"F14.imprint","IMPRINT",FACE,{"disambiguationData":[TD([[makeQuery(id+"F14.imprint","IMPRINT",EDGE,{"derivedFrom":subQ0}),1.0]])]});}
            extrude(context, id + "F16", {"entities" : qUnion([Q0, Q1]), "operationType" : NewBodyOperationType.ADD, "depth" : 1 * mm, "offsetDistance" : 25 * mm});
        }
        {
            var Q0;
            Q0=makeQuery(id+"F16.opExtrude","CAP_EDGE",EDGE,{"disambiguationData":[OSD([sQuery(id+"F14.wireOp",EDGE,"E53")])],"isStart":true});
            var Q1;
            Q1=makeQuery(id+"F16.opExtrude","CAP_EDGE",EDGE,{"disambiguationData":[OSD([sQuery(id+"F14.wireOp",EDGE,"E50.MirrorCS"),sQuery(id+"F14.wireOp",EDGE,"E55")])],"isStart":true});
            var Q2;
            {var subQ0=sQuery(id+"F14.wireOp",EDGE,"E52");var subQ1=sQuery(id+"F14.wireOp",EDGE,"E51");var subQ2=sQuery(id+"F14.wireOp",EDGE,"E50.MirrorCS");Q2=makeQuery(id+"F16.boolean.opBoolean","MERGE",EDGE,{"derivedFrom":[makeQuery(id+"F15.boolean.opBoolean","COPY",EDGE,{"derivedFrom":makeQuery(id+"F15.opExtrude","SWEPT_EDGE",EDGE,{"disambiguationData":[OSD([subQ2,subQ1,subQ0])]})}),makeQuery(id+"F16.opExtrude","SWEPT_EDGE",EDGE,{"disambiguationData":[OSD([subQ2,subQ1,subQ0])]})]});}
            var Q3;
            Q3=makeQuery(id+"F15.boolean.opBoolean","COPY",EDGE,{"derivedFrom":makeQuery(id+"F15.opExtrude","SWEPT_EDGE",EDGE,{"disambiguationData":[OSD([sQuery(id+"F0.wireOp",EDGE,"E33"),sQuery(id+"F14.wireOp",EDGE,"E49"),sQuery(id+"F14.wireOp",EDGE,"E51")])]})});
            fillet(context, id + "F17", {"entities" : qUnion([Q0, Q1, Q2, Q3]), "radius" : 1 * mm, "tangentPropagation" : true, "allowEdgeOverflow" : false});
        }
    });
